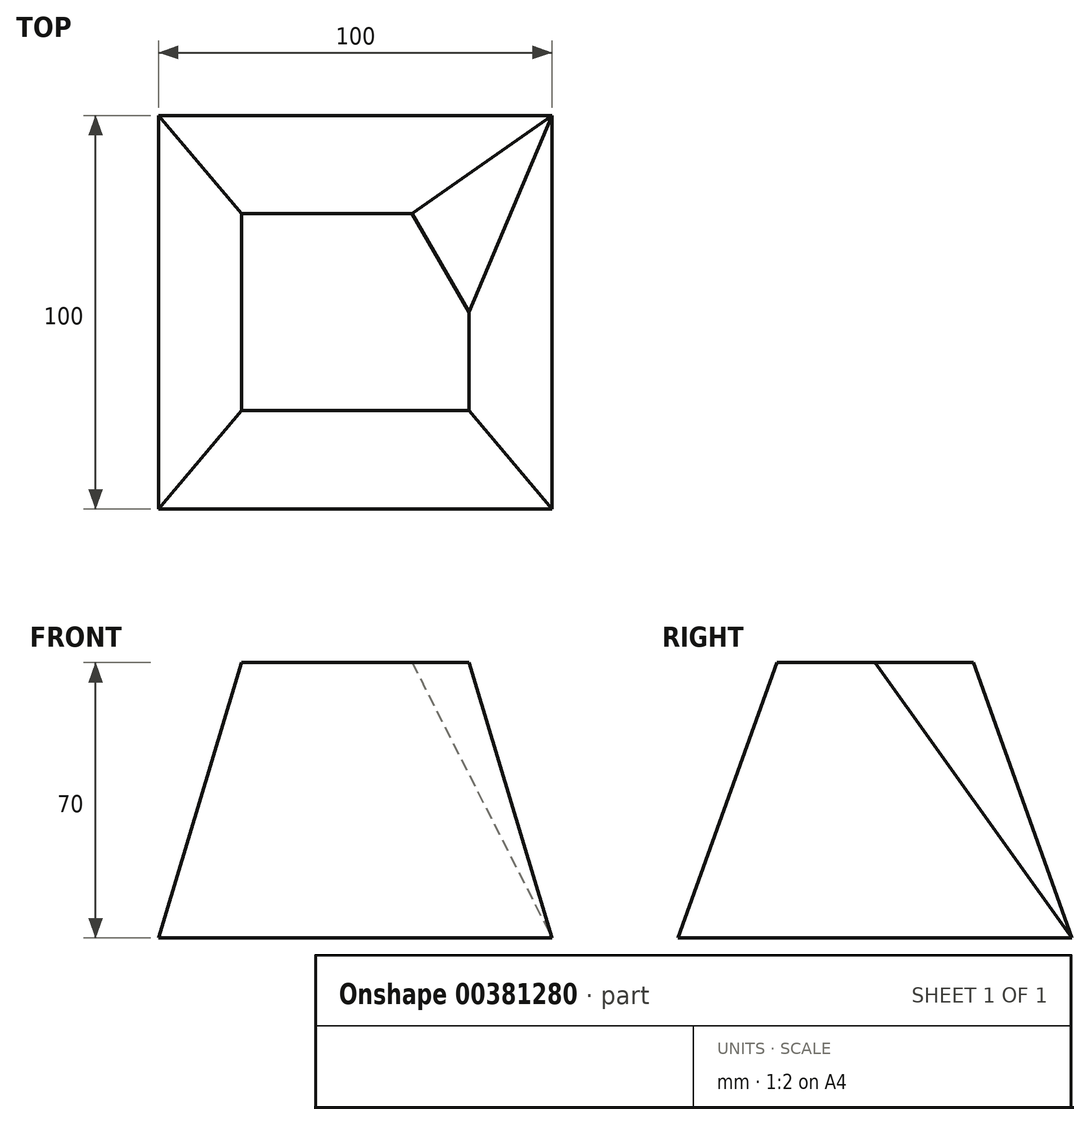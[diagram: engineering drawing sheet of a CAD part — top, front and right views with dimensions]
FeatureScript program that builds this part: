
annotation { "Feature Type Name" : "Feature", "Feature Type Description" : "" }
export const myFeature = defineFeature(function(context is Context, id is Id, definition is map)
    precondition{}
    {
        {
            var Q0;
            Q0=qCreatedBy(makeId("Top.planeOp"),FACE);
            cPlane(context, id + "F0", {"entities" : qUnion([Q0]), "cplaneType" : CPlaneType.OFFSET, "offset" : 70 * mm, "width" : 152.4 * mm, "height" : 152.4 * mm});
        }
        {
            var Q0;
            Q0=qCreatedBy(id+"F0.planeOp",FACE);
            var sketch = newSketch(context, id + "F1", { "sketchPlane" : qUnion([Q0])});
            skCircle(sketch, "E0.cCircle", {"center": v(0, 0) * mm, "radius": 25 * mm, "construction": true});
            skLineSegment(sketch, "E0.0", {"start": v(28.87, 0.11) * mm, "end": v(14.53, -24.94) * mm});
            skLineSegment(sketch, "E0.1", {"start": v(14.53, -24.94) * mm, "end": v(-14.34, -25.06) * mm});
            skLineSegment(sketch, "E0.2", {"start": v(-14.34, -25.06) * mm, "end": v(-28.87, -0.11) * mm});
            skLineSegment(sketch, "E0.3", {"start": v(-28.87, -0.11) * mm, "end": v(-14.53, 24.94) * mm});
            skLineSegment(sketch, "E0.4", {"start": v(-14.53, 24.94) * mm, "end": v(14.34, 25.06) * mm});
            skLineSegment(sketch, "E0.5", {"start": v(14.34, 25.06) * mm, "end": v(28.87, 0.11) * mm});
            skPoint(sketch, "E0.0.midPoint", {"position": v(21.7, -12.42) * mm});
            skSolve(sketch);
        }
        {
            var Q0;
            Q0=qCreatedBy(makeId("Top.planeOp"),FACE);
            var sketch = newSketch(context, id + "F2", { "sketchPlane" : qUnion([Q0])});
            skLineSegment(sketch, "E1.bottom", {"start": v(-50, -50) * mm, "end": v(50, -50) * mm});
            skLineSegment(sketch, "E1.top", {"start": v(-50, 50) * mm, "end": v(50, 50) * mm});
            skLineSegment(sketch, "E1.left", {"start": v(-50, -50) * mm, "end": v(-50, 50) * mm});
            skLineSegment(sketch, "E1.right", {"start": v(50, -50) * mm, "end": v(50, 50) * mm});
            skLineSegment(sketch, "E2", {"start": v(0, -50) * mm, "end": v(0, 50) * mm, "construction": true});
            skSolve(sketch);
        }
        {
            var Q0;
            Q0=qCreatedBy(id+"F0.planeOp",FACE);
            var sketch = newSketch(context, id + "F3", { "sketchPlane" : qUnion([Q0])});
            skLineSegment(sketch, "E3.bottom", {"start": v(-28.87, -24.94) * mm, "end": v(28.87, -24.94) * mm});
            skLineSegment(sketch, "E3.top", {"start": v(-28.87, 25.06) * mm, "end": v(28.87, 25.06) * mm});
            skLineSegment(sketch, "E3.left", {"start": v(-28.87, -24.94) * mm, "end": v(-28.87, 25.06) * mm});
            skLineSegment(sketch, "E3.right", {"start": v(28.87, -24.94) * mm, "end": v(28.87, 25.06) * mm});
            skSolve(sketch);
        }
        {
            var Q0;
            Q0=makeQuery(id+"F3.imprint","IMPRINT",FACE,{"disambiguationData":[TD([[makeQuery(id+"F3.imprint","IMPRINT",EDGE,{"derivedFrom":sQuery(id+"F3.wireOp",EDGE,"E3.bottom")}),1.0]])]});
            var Q1;
            Q1=makeQuery(id+"F2.imprint","IMPRINT",FACE,{"disambiguationData":[TD([[makeQuery(id+"F2.imprint","IMPRINT",EDGE,{"derivedFrom":sQuery(id+"F2.wireOp",EDGE,"E1.bottom")}),1.0]])]});
            loft(context, id + "F4", {"sheetProfilesArray" : [{ "sheetProfileEntities" : qUnion([Q0]) }, { "sheetProfileEntities" : qUnion([Q1]) }]});
        }
        {
            var Q0;
            Q0=qCreatedBy(id+"F0.planeOp",FACE);
            var sketch = newSketch(context, id + "F5", { "sketchPlane" : qUnion([Q0])});
            skLineSegment(sketch, "E4", {"start": v(28.87, 0) * mm, "end": v(14.4, 25.06) * mm});
            skLineSegment(sketch, "E5", {"start": v(14.4, 25.06) * mm, "end": v(28.87, 25.06) * mm});
            skLineSegment(sketch, "E6", {"start": v(28.87, 25.06) * mm, "end": v(28.87, 0) * mm});
            skSolve(sketch);
        }
        {
            var Q1;
            Q1=makeQuery(id+"F5.imprint","IMPRINT",FACE,{"disambiguationData":[TD([[makeQuery(id+"F5.imprint","IMPRINT",EDGE,{"derivedFrom":sQuery(id+"F5.wireOp",EDGE,"E4")}),-1.0]])]});
            var Q2;
            Q2=makeQuery(id+"F4.opLoft","MID_CAP_VERTEX",VERTEX,{"disambiguationData":[OSD([sQuery(id+"F2.wireOp",EDGE,"E1.top"),sQuery(id+"F2.wireOp",EDGE,"E1.right")])],"capPos":1.0});
            loft(context, id + "F6", {"operationType" : NewBodyOperationType.ADD, "sheetProfilesArray" : [{ "sheetProfileEntities" : qUnion([Q1]) }, { "sheetProfileEntities" : qUnion([Q2]) }]});
        }
        {
            var Q1;
            Q1=makeQuery(id+"F5.imprint","IMPRINT",FACE,{"disambiguationData":[TD([[makeQuery(id+"F5.imprint","IMPRINT",EDGE,{"derivedFrom":sQuery(id+"F5.wireOp",EDGE,"E4")}),-1.0]])]});
            var Q2;
            Q2=makeQuery(id+"F4.opLoft","MID_CAP_VERTEX",VERTEX,{"disambiguationData":[OSD([sQuery(id+"F2.wireOp",EDGE,"E1.top"),sQuery(id+"F2.wireOp",EDGE,"E1.right")])],"capPos":1.0});
            loft(context, id + "F7", {"operationType" : NewBodyOperationType.REMOVE, "sheetProfilesArray" : [{ "sheetProfileEntities" : qUnion([Q1]) }, { "sheetProfileEntities" : qUnion([Q2]) }]});
        }
    });
